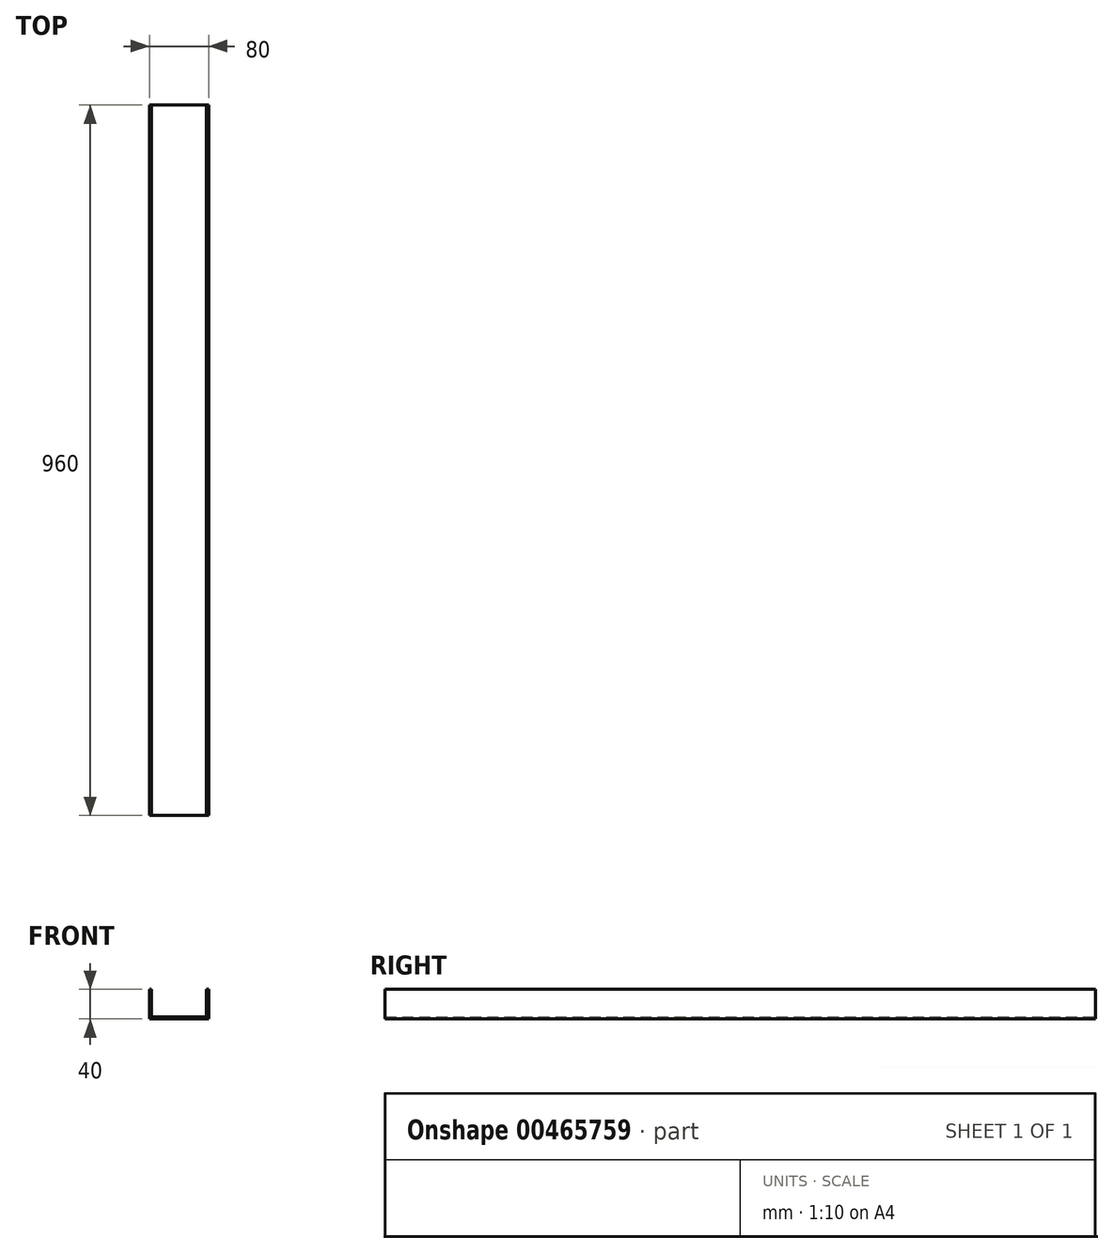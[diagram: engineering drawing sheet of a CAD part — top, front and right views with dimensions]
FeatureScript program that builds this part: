
annotation { "Feature Type Name" : "Feature", "Feature Type Description" : "" }
export const myFeature = defineFeature(function(context is Context, id is Id, definition is map)
    precondition{}
    {
        {
            var Q0;
            Q0=qCreatedBy(makeId("Front.planeOp"),FACE);
            var sketch = newSketch(context, id + "F0", { "sketchPlane" : qUnion([Q0])});
            skLineSegment(sketch, "E0", {"start": v(-8, 0) * mm, "end": v(-8, 40) * mm});
            skLineSegment(sketch, "E1", {"start": v(-8, 0) * mm, "end": v(72, 0) * mm});
            skLineSegment(sketch, "E2", {"start": v(72, 0) * mm, "end": v(72, 40) * mm});
            skLineSegment(sketch, "E3", {"start": v(72, 40) * mm, "end": v(69, 40) * mm});
            skLineSegment(sketch, "E4", {"start": v(69, 40) * mm, "end": v(69, 3) * mm});
            skLineSegment(sketch, "E5", {"start": v(-8, 40) * mm, "end": v(-5, 40) * mm});
            skLineSegment(sketch, "E6", {"start": v(-5, 40) * mm, "end": v(-5, 3) * mm});
            skLineSegment(sketch, "E7", {"start": v(-5, 3) * mm, "end": v(69, 3) * mm});
            skSolve(sketch);
        }
        {
            var Q0;
            Q0 = qSketchRegion(id + "F0", true);
            extrude(context, id + "F1", {"entities" : qUnion([Q0]), "depth" : 960 * mm, "offsetDistance" : 25 * mm});
        }
    });
